# Revit family: SH-45
name_source: partatom
category: Устройства связи
revit_build: Autodesk Revit 2016 (Build: 20160314_0715(x64)
units: mm (PartAtom-declared; Revit-internal decimal feet)

## family parameters
Всегда вертикально = Нет
На основе рабочей плоскости = Да
Общий = Да
При загрузке вырезать с полостями = Нет
Размер круглого соединителя = Использовать диаметр
Сохранять ориентацию аннотаций = Нет
Тип детали = Нормальный
Точка расчета площади = Нет

## types (1)
- SH-45
    ADSK_URL документации изделия = http://cdn.bas-ip.com
    ADSK_URL страницы изделия = https://www.bas-ip.ru
    ADSK_Версия Revit = Revit 2016
    ADSK_Единица измерения = шт
    ADSK_Завод-изготовитель = BAS-IP
    ADSK_Классификация нагрузок = Кнопка выхода
    ADSK_Количество фаз = 1
    ADSK_Коэффициент мощности = 0.9
    ADSK_Марка = SH-45
    ADSK_Наименование = КНОПКА ВЫХОДА SH-45
    ADSK_Наименование краткое = SH-45
    ADSK_Напряжение = 12 В
    ADSK_Номинальная мощность = 0 Вт
    ADSK_Полная мощность = 0 В·А
    ADSK_Размер_Длина = 70 мм
    ADSK_Размер_Толщина = 20 мм
    ADSK_Размер_Ширина = 114 мм
    BIM library = https://bimlib.ru
    URL = https://www.bas-ip.ru
    Группа модели = Кнопка выхода
    Дополнительно = Возможность изменение цвета подсветки, Триггерный режим, Накладка из нержавеющей стали
    Допустимая влажность = 10 – 90%
    Изготовитель = BAS-IP
    Изображение = SHV_Изображение_SH-45
    Изображение типоразмера = <Нет>
    Класс степени защиты = IP68
    Материал корпуса = SHV_Сталь
    Напряжение питания = 12 В
    Описание = Кнопка выхода SH-45 выполнена из прочной нержавеющей стали и имеет практически неограниченный ресурс нажатий – более 50 млн
    Отметка по умолчанию = 0 мм
    Размеры = 70х114х19,5 мм
    Ресурс работы = Более 50 миллионов нажатий
    Температурный режим = -40 ... +60 °C
